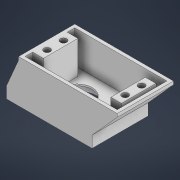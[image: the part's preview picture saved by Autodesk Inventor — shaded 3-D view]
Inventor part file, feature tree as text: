
AUTODESK INVENTOR PART (.ipt)
format: ipt  version: 2021 (Build 250183000, 183)  size: 425,472 bytes
history: native  units: mm
features: extrude x12, sketch x11, other x3, plane x1, loft x1, shell x1
ambient origin geometry x8: Origin, YZ Plane, XZ Plane, XY Plane, X Axis, Y Axis, Z Axis, Center Point
bodies: Volumenkörper1 (feature_tree)
feature tree (29):
  extrude  "Extrusion1"  Depth=34.2mm
  plane  "Arbeitsebene1"
  extrude  "Extrusion2"  Depth=17.0mm
  loft  "Erhebung1"
  shell  "Wandung1"  Thickness=7.3mm
  extrude  "Extrusion5"  TaperAngle=0.0deg  [1 undecoded]
  sketch  "Skizze11"  dims[d8=2.0mm d9=0.0mm d15=0.0mm d16=90.0deg]
  extrude  "Extrusion9"  Depth=2.0mm
  other  "Verdickung1"
  extrude  "Extrusion11"  Depth=4.0mm TaperAngle=0.0deg
  extrude  "Extrusion12"  Depth=21.0mm
  extrude  "Extrusion13"  Depth=1.0mm
  extrude  "Extrusion14"  Depth=6.5mm
  extrude  "Extrusion15"  Depth=21.0mm TaperAngle=0.0deg
  extrude  "Extrusion18"  Depth=10.0mm
  extrude  "Extrusion16"  Depth=10.0mm
  extrude  "Extrusion17"  Depth=5.0mm
  sketch  "Skizze1"  dims[d0=52.0mm d1=34.2mm]
  sketch  "Skizze2"  dims[d2=7.0mm d3=0.0mm d4=17.0mm]
  other  "Kanten1"
  other  "Kanten2"
  sketch  "Skizze7"  dims[d5=60.0mm d6=34.2mm d7=7.3mm]
  sketch  "Skizze13"  dims[d17=0.0mm d18=90.0deg d19=2.0mm]
  sketch  "Skizze14"  dims[d28=2.0mm d29=4.0mm d30=0.0mm]
  sketch  "Skizze15"  dims[d49=6.5mm d50=21.0mm]
  sketch  "Skizze16"  dims[d51=6.0mm d52=0.0mm d56=1.0mm]
  sketch  "Skizze17"  dims[d57=1.0mm d58=6.5mm]
  sketch  "Skizze18"  dims[d59=21.0mm d60=12.0mm d61=0.0mm]
  sketch  "Skizze19"  dims[d65=3.9mm d66=3.25mm d67=3.9mm d68=5.0mm d69=5.0mm d70=3.25mm d71=3.9mm d72=3.25mm d73=5.0mm d74=3.9mm d75=3.25mm d76=5.0mm d77=5.7mm d78=0.0mm d79=6.0mm d80=0.0mm d81=24.2mm d82=5.0mm d83=0.0mm d84=18.0mm d85=5.0mm d86=0.0mm d87=10.5mm d88=8.5mm d95=10.0mm d96=0.0mm d97=3.0mm d98=11.0mm d99=7.0mm d100=18.0mm d101=11.0mm d102=18.0mm d103=10.0mm d104=0.0mm d105=10.0mm d106=0.0mm d31=0.872665mm]
note: 1 required parameter value undecoded (feature->parameter linkage not recoverable at this tier; creation-order binding heuristic only, values carry confidence <= 0.55)
